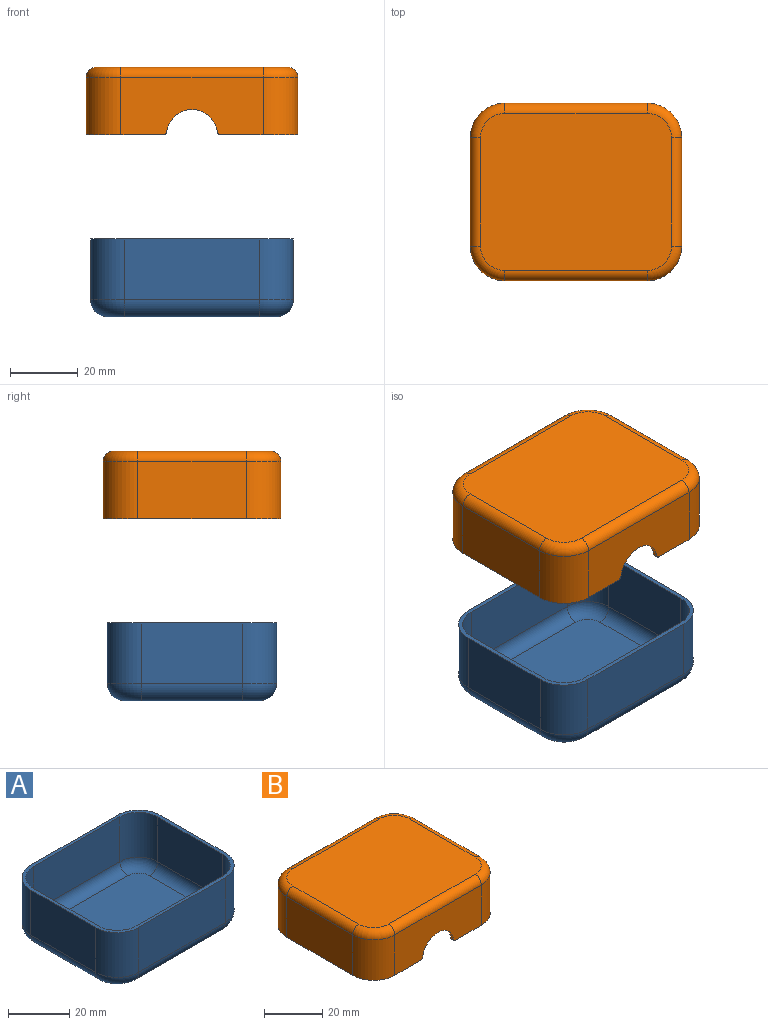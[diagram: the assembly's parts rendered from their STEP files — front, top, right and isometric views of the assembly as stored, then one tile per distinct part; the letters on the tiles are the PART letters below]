
ASSEMBLY  parts=2 mates=2
PART A: 35 faces, bbox 61.6x51.6x23 mm
  f0: plane 60x50mm, normal (0,0,1), area 248.6mm2, adj f1,f2,f3,f4,f5,f6,f7,f8
  f1: plane 30x18mm, normal (1,0,0), area 540mm2, adj f0,f2,f8,f14
  f2: cylinder r=10mm len=18mm, axis (0,0,-1), area 282.7mm2, adj f0,f1,f3,f16
  f3: plane 40x18mm, normal (0,1,0), area 720mm2, adj f0,f2,f4,f17
  f4: cylinder r=10mm len=18mm, axis (0,0,-1), area 282.7mm2, adj f0,f3,f5,f15
  f5: plane 30x18mm, normal (-1,0,0), area 540mm2, adj f0,f4,f6,f13
  f6: cylinder r=10mm len=18mm, axis (0,0,-1), area 282.7mm2, adj f0,f5,f7,f11
  f7: plane 40x18mm, normal (0,-1,0), area 720mm2, adj f0,f6,f8,f10
  f8: cylinder r=10mm len=18mm, axis (0,0,-1), area 282.7mm2, adj f0,f1,f7,f12
  f9: plane 50x40mm, normal (0,0,-1), area 1978.5mm2, adj f10,f11,f12,f13,f14,f15,f16,f17
  f10: cylinder r=5mm len=40mm, axis (1,0,0), area 314.2mm2, adj f7,f9,f11,f12
  f11: torus R=5mm, axis (0,0,1), area 101mm2, adj f6,f9,f10,f13
  f12: torus R=5mm, axis (0,0,1), area 101mm2, adj f8,f9,f10,f14
  f13: cylinder r=5mm len=30mm, axis (0,-1,0), area 235.6mm2, adj f5,f9,f11,f15
  f14: cylinder r=5mm len=30mm, axis (0,1,0), area 235.6mm2, adj f1,f9,f12,f16
  f15: torus R=5mm, axis (0,0,1), area 101mm2, adj f4,f9,f13,f17
  f16: torus R=5mm, axis (0,0,1), area 101mm2, adj f2,f9,f14,f17
  f17: cylinder r=5mm len=40mm, axis (-1,0,0), area 314.2mm2, adj f3,f9,f15,f16
  f18: plane 30x18mm, normal (-1,0,0), area 540mm2, adj f0,f19,f25,f31
  f19: cylinder r=8.75mm len=18mm, axis (0,0,-1), area 247.4mm2, adj f0,f18,f20,f33
  f20: plane 40x18mm, normal (0,-1,0), area 720mm2, adj f0,f19,f21,f34
  f21: cylinder r=8.75mm len=18mm, axis (0,0,-1), area 247.4mm2, adj f0,f20,f22,f32
  f22: plane 30x18mm, normal (1,0,0), area 540mm2, adj f0,f21,f23,f30
  f23: cylinder r=8.75mm len=18mm, axis (0,0,-1), area 247.4mm2, adj f0,f22,f24,f28
  f24: plane 40x18mm, normal (0,1,0), area 720mm2, adj f0,f23,f25,f27
  f25: cylinder r=8.75mm len=18mm, axis (0,0,-1), area 247.4mm2, adj f0,f18,f24,f29
  f26: plane 50x40mm, normal (0,0,1), area 1978.5mm2, adj f27,f28,f29,f30,f31,f32,f33,f34
  f27: cylinder r=3.75mm len=40mm, axis (1,0,0), area 235.6mm2, adj f24,f26,f28,f29
  f28: torus R=5mm, axis (0,0,1), area 68.4mm2, adj f23,f26,f27,f30
  f29: torus R=5mm, axis (0,0,1), area 68.4mm2, adj f25,f26,f27,f31
  f30: cylinder r=3.75mm len=30mm, axis (0,-1,0), area 176.7mm2, adj f22,f26,f28,f32
  f31: cylinder r=3.75mm len=30mm, axis (0,1,0), area 176.7mm2, adj f18,f26,f29,f33
  f32: torus R=5mm, axis (0,0,1), area 68.4mm2, adj f21,f26,f30,f34
  f33: torus R=5mm, axis (0,0,1), area 68.4mm2, adj f19,f26,f31,f34
  f34: cylinder r=3.75mm len=40mm, axis (-1,0,0), area 235.6mm2, adj f20,f26,f32,f33
PART B: 42 faces, bbox 64.2x54.2x20 mm
  f0: plane 52.5x22.81mm, normal (0,0,-1), area 109.2mm2, adj f1,f5,f6,f7,f8,f21,f22,f23
  f1: plane 42x17mm, normal (0,-1,0), area 625.3mm2, adj f0,f2,f8,f9,f11,f36,f40,f41
  f2: plane 52.5x22.81mm, normal (0,0,-1), area 109.2mm2, adj f1,f3,f4,f5,f9,f19,f20,f21
  f3: plane 32x17mm, normal (1,0,0), area 544mm2, adj f2,f4,f9,f15
  f4: cylinder r=10.25mm len=17mm, axis (0,0,-1), area 273.7mm2, adj f2,f3,f5,f17
  f5: plane 42x17mm, normal (0,1,0), area 625.3mm2, adj f0,f2,f4,f6,f18,f37,f38,f39
  f6: cylinder r=10.25mm len=17mm, axis (0,0,-1), area 273.7mm2, adj f0,f5,f7,f16
  f7: plane 32x17mm, normal (-1,0,0), area 544mm2, adj f0,f6,f8,f14
  f8: cylinder r=10.25mm len=17mm, axis (0,0,-1), area 273.7mm2, adj f0,f1,f7,f12
  f9: cylinder r=10.25mm len=17mm, axis (0,0,-1), area 273.7mm2, adj f1,f2,f3,f13
  f10: plane 56.5x46.5mm, normal (0,0,1), area 2582.1mm2, adj f11,f12,f13,f14,f15,f16,f17,f18
  f11: cylinder r=3mm len=42mm, axis (-1,0,0), area 197.9mm2, adj f1,f10,f12,f13
  f12: torus R=7.25mm, axis (0,0,1), area 67.8mm2, adj f8,f10,f11,f14
  f13: torus R=7.25mm, axis (0,0,1), area 67.8mm2, adj f9,f10,f11,f15
  f14: cylinder r=3mm len=32mm, axis (0,1,0), area 150.8mm2, adj f7,f10,f12,f16
  f15: cylinder r=3mm len=32mm, axis (0,-1,0), area 150.8mm2, adj f3,f10,f13,f17
  f16: torus R=7.25mm, axis (0,0,1), area 67.8mm2, adj f6,f10,f14,f18
  f17: torus R=7.25mm, axis (0,0,1), area 67.8mm2, adj f4,f10,f15,f18
  f18: cylinder r=3mm len=42mm, axis (1,0,0), area 197.9mm2, adj f5,f10,f16,f17
  f19: plane 32x17mm, normal (-1,0,0), area 544mm2, adj f2,f20,f26,f32
  f20: cylinder r=9mm len=17mm, axis (0,0,-1), area 240.3mm2, adj f2,f19,f21,f34
  f21: plane 42x17mm, normal (0,-1,0), area 625.3mm2, adj f0,f2,f20,f22,f35,f37,f38,f39
  f22: cylinder r=9mm len=17mm, axis (0,0,-1), area 240.3mm2, adj f0,f21,f23,f33
  f23: plane 32x17mm, normal (1,0,0), area 544mm2, adj f0,f22,f24,f31
  f24: cylinder r=9mm len=17mm, axis (0,0,-1), area 240.3mm2, adj f0,f23,f25,f29
  f25: plane 42x17mm, normal (0,1,0), area 625.3mm2, adj f0,f2,f24,f26,f28,f36,f40,f41
  f26: cylinder r=9mm len=17mm, axis (0,0,-1), area 240.3mm2, adj f2,f19,f25,f30
  f27: plane 56.5x46.5mm, normal (0,0,-1), area 2582.1mm2, adj f28,f29,f30,f31,f32,f33,f34,f35
  f28: cylinder r=1.75mm len=42mm, axis (-1,0,0), area 115.5mm2, adj f25,f27,f29,f30
  f29: torus R=7.25mm, axis (0,0,1), area 36.1mm2, adj f24,f27,f28,f31
  f30: torus R=7.25mm, axis (0,0,1), area 36.1mm2, adj f26,f27,f28,f32
  f31: cylinder r=1.75mm len=32mm, axis (0,1,0), area 88mm2, adj f23,f27,f29,f33
  f32: cylinder r=1.75mm len=32mm, axis (0,-1,0), area 88mm2, adj f19,f27,f30,f34
  f33: torus R=7.25mm, axis (0,0,1), area 36.1mm2, adj f22,f27,f31,f35
  f34: torus R=7.25mm, axis (0,0,1), area 36.1mm2, adj f20,f27,f32,f35
  f35: cylinder r=1.75mm len=42mm, axis (1,0,0), area 115.5mm2, adj f21,f27,f33,f34
  f36: cylinder r=7.5mm len=14.9mm, axis (0,-1,0), area 27.2mm2, adj f1,f25,f40,f41
  f37: cylinder r=7.5mm len=14.9mm, axis (0,-1,0), area 27.2mm2, adj f5,f21,f38,f39
  f38: cylinder r=1mm len=1.25mm, axis (0,-1,0), area 1.8mm2, adj f0,f5,f21,f37
  f39: cylinder r=1mm len=1.25mm, axis (0,-1,0), area 1.8mm2, adj f2,f5,f21,f37
  f40: cylinder r=1mm len=1.25mm, axis (0,-1,0), area 1.8mm2, adj f0,f1,f25,f36
  f41: cylinder r=1mm len=1.25mm, axis (0,-1,0), area 1.8mm2, adj f1,f2,f25,f36
PLACE A at identity fixed
PLACE B t=(-1.25,1.25,53.78)mm
MATE planar B.f23 <-> A.f5  axis (1,0,0) through (0,-25,62.28)mm
MATE planar A.f7 <-> B.f25  axis (0,-1,0) through (30,-50,14)mm
